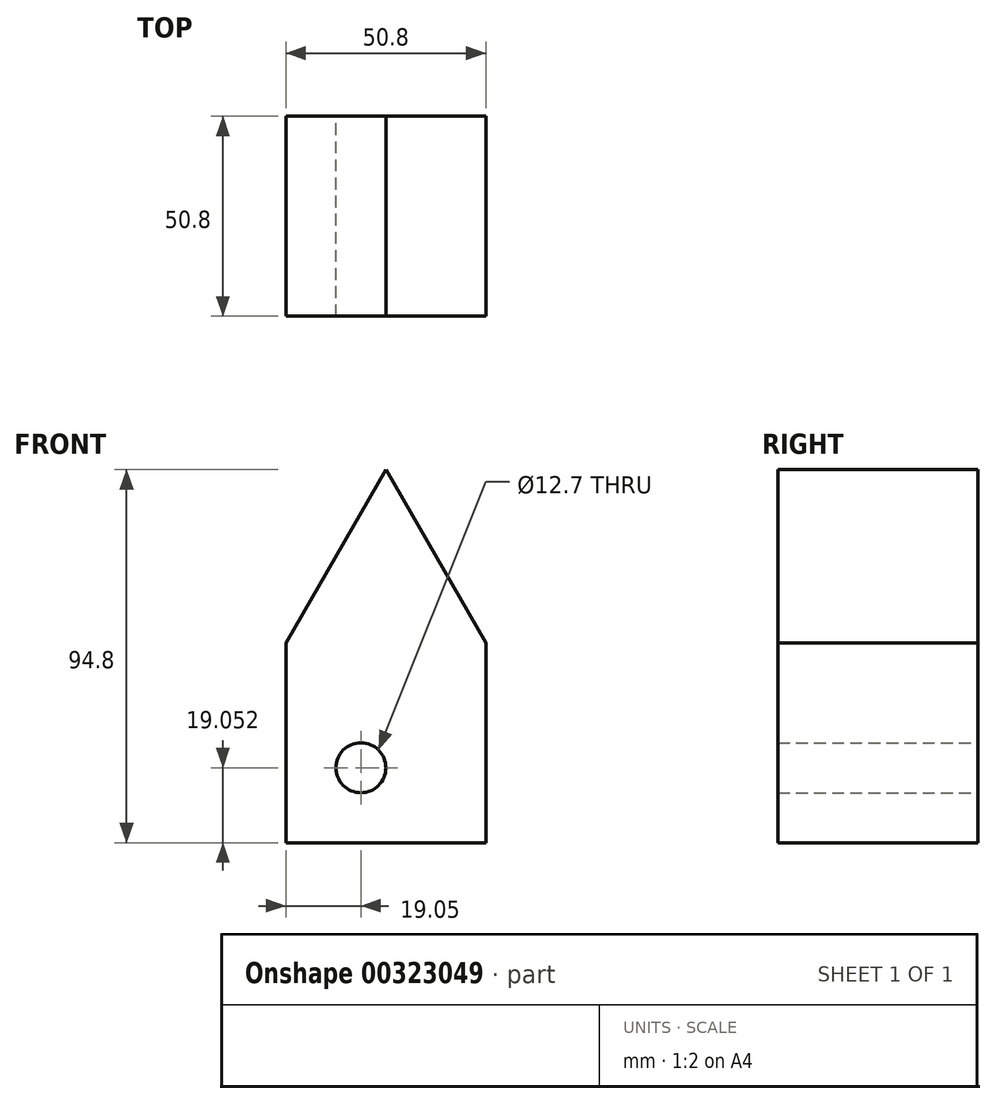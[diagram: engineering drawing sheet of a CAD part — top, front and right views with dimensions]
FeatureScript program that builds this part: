
annotation { "Feature Type Name" : "Feature", "Feature Type Description" : "" }
export const myFeature = defineFeature(function(context is Context, id is Id, definition is map)
    precondition{}
    {
        {
            var Q0;
            Q0=qCreatedBy(makeId("Front.planeOp"),FACE);
            var sketch = newSketch(context, id + "F0", { "sketchPlane" : qUnion([Q0])});
            skLineSegment(sketch, "E0.top", {"start": v(-8.67, -26.52) * mm, "end": v(42.13, -26.52) * mm});
            skLineSegment(sketch, "E0.left", {"start": v(-8.67, 24.28) * mm, "end": v(-8.67, -26.52) * mm});
            skLineSegment(sketch, "E0.right", {"start": v(42.13, 24.28) * mm, "end": v(42.13, -26.52) * mm});
            skLineSegment(sketch, "E1", {"start": v(-8.67, 24.28) * mm, "end": v(16.73, 68.28) * mm});
            skLineSegment(sketch, "E2", {"start": v(42.13, 24.28) * mm, "end": v(16.73, 68.28) * mm});
            skCircle(sketch, "E3", {"center": v(10.38, -7.47) * mm, "radius": 6.35 * mm});
            skSolve(sketch);
        }
        {
            var Q0;
            Q0=makeQuery(id+"F0.imprint","IMPRINT",FACE,{"disambiguationData":[TD([[makeQuery(id+"F0.imprint","IMPRINT",EDGE,{"derivedFrom":sQuery(id+"F0.wireOp",EDGE,"E0.top")}),1.0]])]});
            extrude(context, id + "F1", {"entities" : qUnion([Q0]), "depth" : 50.8 * mm});
        }
    });
